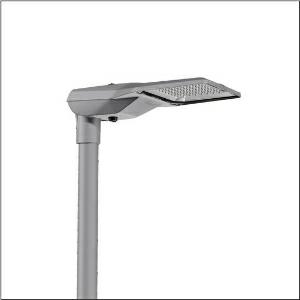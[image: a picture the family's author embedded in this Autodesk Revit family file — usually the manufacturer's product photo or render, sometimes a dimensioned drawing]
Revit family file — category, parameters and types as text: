
# Revit family: streetlight_sl_21_iq_midi___st1_0ab_5xe3m31y08mb_ceed
name_source: partatom
category: Lighting Fixtures
units: mm (PartAtom-declared; Revit-internal decimal feet)

## family parameters
Cut with Voids When Loaded = No
Host = Face
Light Source = No
Part Type = Normal
Room Calculation Point = No
Round Connector Dimension = Use Diameter
Shared = No

## types (1)
- --- (1 x LED, 16140 lm, 129.3 W, 3000K)
    Apparent Load = 129 VA
    CIE Flux Codes = 38 73 97 100 100
    Color Rendering = 70
    Color Temperature = 3000K
    Default Elevation = 1800 mm
    Description = Streetlight SL 21 iQ midi, mast luminaire, primary light control with lens, of PMMA, primary optical cover: cover, of toughened safety glass, transparent, light distribution: ST1.0aB, light emission: direct distribution, primary light characteristic: asymmetric, installation type: post-top, side-entry, LED, High Power LED, rated luminous flux: 16.140lm, luminous efficacy: 125lm/W, light colour: 730, colour temperature: 3000K, control gear: iQ-Street Remote, D4i with power reduction, control: pre-setting: logarithmic dimming characteristic, Street-Remote, Auto-Match, Temp-Guard, Lumen-Switch, Night-Set, Smart-Wire, Light-Fading, Desk-Remote (wireless, voltage-free reading and setting of iQ features in the workshop via application-optimized NFC function/RFID function), optimised constant luminous flux control (CLO 2.0), mains connection: 230..240V, AC, 50/60Hz, start of lifetime: 129W, end of service life: 142W, reduction: 56W, luminaire housing, of diecast aluminium, powder-coated, SITECO metallic grey (DB 702S), corrosivity category C5 high according to DIN EN ISO 12944, please order mast flange separately, inclination adjustable: 0°, 5°, 10°, 15°, sealing non-destructively replaceable, multi-level sealing system, length: 644mm, width: 335mm, height: 110mm, mast flange for spigot size: 42mm (side-entry): 5XC10008XM4, 60/48mm (side-entry/post-top): 5XC10108XM2, 76/60mm (side-entry/post-top): 5XC10108XM1, mounting height: 4..8m, Smart Interface below and above, protection rating (complete): IP66, insulation class (complete): insulation class II (safety insulation), certification: CE, ENEC, ENEC+, VDE, impact resistance: IK10, permissible operating ambient temperature for outdoor applications: -40..+50°C, standard-compliant lighting for roads and squares, packaging unit: 1 piece

Light Distribution: ST1.0aB
    Height = 111 mm
    Lamp = 1 x LED
    Lamp Light Flux = 16140 lm
    Lamp Power = 129.3 W
    Lamp count = 1
    Length = 644 mm
    Luminous efficacy = 125 lm/W
    Manufacturer = Siteco
    ModVariant = No
    Model = 5XE3M31Y08MB
    Number of Poles = 1
    OnlyDefault = Yes
    Power Factor = 1
    Product Name = Streetlight SL 21 iQ midi | ST1.0aB
    Product group = mast luminaire | pylon top
    ProductGroupID = 6100
    Protection Class = Protection class II
    Protection Degree = IP 66
    RLX_Detail_Level = 1
    RLX_Emergency_Light_Flux = 0 lm
    RLX_Emergency_Type = 0
    RLX_Emergency_Type_DB = No
    RlxData = <blob elided: 90857 chars, md5=7973909b>
    Socket = socket
    Standby Power = 0 W
    System Light Flux = 16141 lm
    System Power = 129 W
    Type Comments = factory setting: luminous flux: 100 % | dim-lin: 254 | 672 mA
    Type Image = l_1004304.jpg
    URL = http://relux.com
    VarID = @adj_112277
    Voltage = 0 V
    Weight = 0.00 kg
    Width = 336 mm

## geometry (parser evidence)
native form markers: Blend x4, Sweep x12
no freeform markers — native parametric forms only
